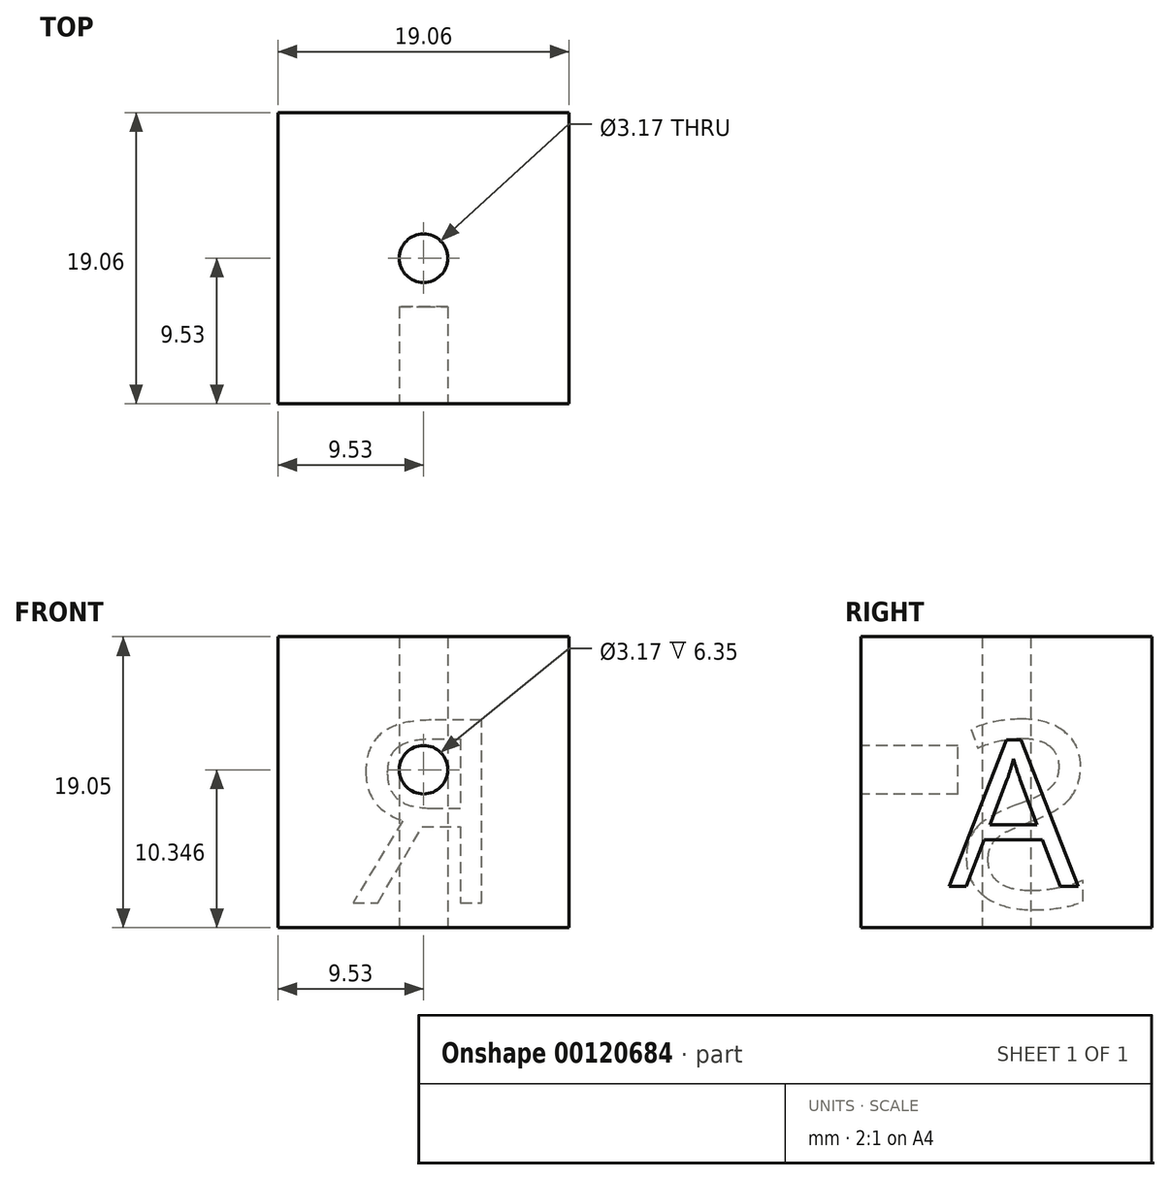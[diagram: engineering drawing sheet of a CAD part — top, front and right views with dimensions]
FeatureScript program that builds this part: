
annotation { "Feature Type Name" : "Feature", "Feature Type Description" : "" }
export const myFeature = defineFeature(function(context is Context, id is Id, definition is map)
    precondition{}
    {
        {
            var Q0;
            Q0=qCreatedBy(makeId("Top.planeOp"),FACE);
            var sketch = newSketch(context, id + "F0", { "sketchPlane" : qUnion([Q0])});
            skLineSegment(sketch, "E0.bottom", {"start": v(9.53, -9.52) * mm, "end": v(-9.52, -9.53) * mm});
            skLineSegment(sketch, "E0.top", {"start": v(9.52, 9.53) * mm, "end": v(-9.53, 9.52) * mm});
            skLineSegment(sketch, "E0.left", {"start": v(9.53, -9.52) * mm, "end": v(9.52, 9.53) * mm});
            skLineSegment(sketch, "E0.right", {"start": v(-9.52, -9.53) * mm, "end": v(-9.53, 9.52) * mm});
            skPoint(sketch, "E0.middle", {"position": v(0, 0) * mm});
            skSolve(sketch);
        }
        {
            var Q0;
            Q0 = qSketchRegion(id + "F0", true);
            extrude(context, id + "F1", {"entities" : qUnion([Q0]), "depth" : 19.05 * mm});
        }
        {
            var Q0;
            Q0=makeQuery(id+"F0.imprint","IMPRINT",FACE,{"disambiguationData":[TD([[makeQuery(id+"F0.imprint","IMPRINT",EDGE,{"derivedFrom":sQuery(id+"F0.wireOp",EDGE,"E0.bottom")}),-1.0]])]});
            var sketch = newSketch(context, id + "F2", { "sketchPlane" : qUnion([Q0])});
            skCircle(sketch, "E1", {"center": v(0, 0) * mm, "radius": 1.59 * mm});
            skSolve(sketch);
        }
        {
            var Q0;
            Q0=makeQuery(id+"F2.imprint","IMPRINT",FACE,{"disambiguationData":[TD([[makeQuery(id+"F2.imprint","IMPRINT",EDGE,{"derivedFrom":sQuery(id+"F2.wireOp",EDGE,"E1")}),1.0]])]});
            extrude(context, id + "F3", {"entities" : qUnion([Q0]), "operationType" : NewBodyOperationType.REMOVE, "depth" : 25.4 * mm});
        }
        {
            var Q0;
            Q0=makeQuery(id+"F1.opExtrude","SWEPT_FACE",FACE,{"disambiguationData":[OSD([sQuery(id+"F0.wireOp",EDGE,"E0.bottom")])]});
            var sketch = newSketch(context, id + "F4", { "sketchPlane" : qUnion([Q0])});
            skCircle(sketch, "E2", {"center": v(0, 10.35) * mm, "radius": 1.59 * mm});
            skSolve(sketch);
        }
        {
            var Q0;
            Q0=makeQuery(id+"F4.imprint","IMPRINT",FACE,{"disambiguationData":[TD([[makeQuery(id+"F4.imprint","IMPRINT",EDGE,{"derivedFrom":sQuery(id+"F4.wireOp",EDGE,"E2")}),1.0]])]});
            extrude(context, id + "F5", {"entities" : qUnion([Q0]), "operationType" : NewBodyOperationType.REMOVE, "oppositeDirection" : true, "depth" : 6.35 * mm});
        }
        {
            var Q0;
            Q0=makeQuery(id+"F1.opExtrude","SWEPT_FACE",FACE,{"disambiguationData":[OSD([sQuery(id+"F0.wireOp",EDGE,"E0.left")])]});
            var sketch = newSketch(context, id + "F6", { "sketchPlane" : qUnion([Q0])});
            skText(sketch, "E3", { "text": "A", "fontName": "OpenSans-Regular.ttf"});
            const initialGuessF6  = {"E3": [-0.00375, 0.00272, 1, 0, 0.00961]};
            skSetInitialGuess(sketch, initialGuessF6);
            skSolve(sketch);
        }
        {
            var Q0;
            Q0=makeQuery(id+"F6.imprint","IMPRINT",FACE,{"disambiguationData":[TD([[makeQuery(id+"F6.imprint","IMPRINT",EDGE,{"derivedFrom":sQuery(id+"F6.wireOp",EDGE,"E3.sketch_text.stroke-0")}),-1.0]])]});
            extrude(context, id + "F7", {"entities" : qUnion([Q0]), "operationType" : NewBodyOperationType.REMOVE, "oppositeDirection" : true, "depth" : 1 / 812.8 * mm});
        }
        {
            var Q0;
            Q0=makeQuery(id+"F1.opExtrude","SWEPT_FACE",FACE,{"disambiguationData":[OSD([sQuery(id+"F0.wireOp",EDGE,"E0.top")])]});
            var sketch = newSketch(context, id + "F8", { "sketchPlane" : qUnion([Q0])});
            skText(sketch, "E4", { "text": "R", "fontName": "OpenSans-Regular.ttf"});
            const initialGuessF8  = {"E4": [-0.00544, 0.00164, 1, 0, 0.01205]};
            skSetInitialGuess(sketch, initialGuessF8);
            skSolve(sketch);
        }
        {
            var Q0;
            Q0=makeQuery(id+"F8.imprint","IMPRINT",FACE,{"disambiguationData":[TD([[makeQuery(id+"F8.imprint","IMPRINT",EDGE,{"derivedFrom":sQuery(id+"F8.wireOp",EDGE,"E4.sketch_text.stroke-0")}),-1.0]])]});
            extrude(context, id + "F9", {"entities" : qUnion([Q0]), "operationType" : NewBodyOperationType.REMOVE, "oppositeDirection" : true, "depth" : 1 / 812.8 * mm});
        }
        {
            var Q0;
            Q0=makeQuery(id+"F1.opExtrude","SWEPT_FACE",FACE,{"disambiguationData":[OSD([sQuery(id+"F0.wireOp",EDGE,"E0.right")])]});
            var sketch = newSketch(context, id + "F10", { "sketchPlane" : qUnion([Q0])});
            skText(sketch, "E5", { "text": "S", "fontName": "OpenSans-Regular.ttf"});
            const initialGuessF10  = {"E5": [-0.0059, 0.00135, 1, 0, 0.01224]};
            skSetInitialGuess(sketch, initialGuessF10);
            skSolve(sketch);
        }
        {
            var Q0;
            Q0=makeQuery(id+"F10.imprint","IMPRINT",FACE,{"disambiguationData":[TD([[makeQuery(id+"F10.imprint","IMPRINT",EDGE,{"derivedFrom":sQuery(id+"F10.wireOp",EDGE,"E5.sketch_text.stroke-0")}),-1.0]])]});
            extrude(context, id + "F11", {"entities" : qUnion([Q0]), "operationType" : NewBodyOperationType.REMOVE, "oppositeDirection" : true, "depth" : 1 / 812.8 * mm});
        }
    });
